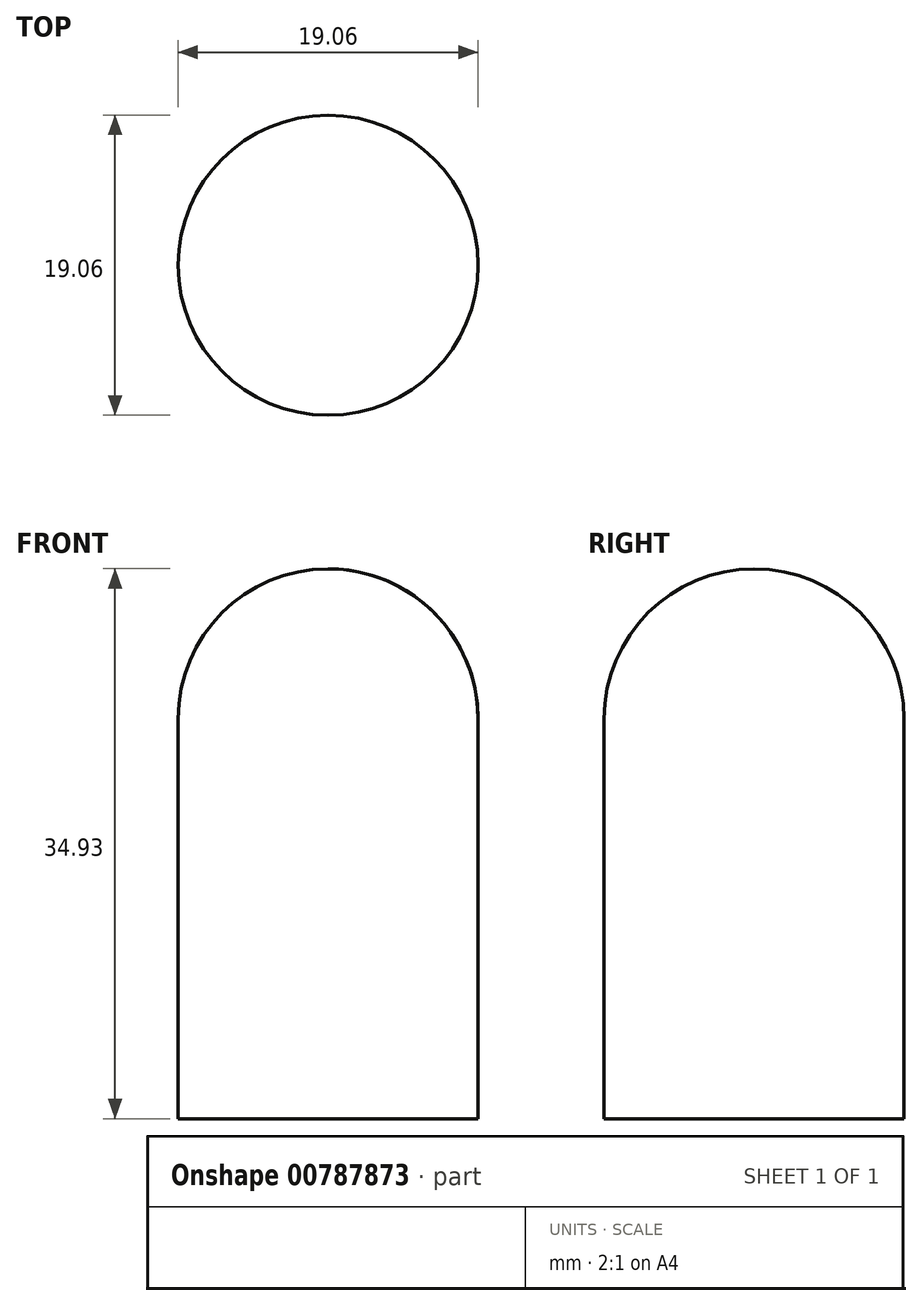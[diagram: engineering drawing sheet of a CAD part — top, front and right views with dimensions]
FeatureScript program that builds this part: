
annotation { "Feature Type Name" : "Feature", "Feature Type Description" : "" }
export const myFeature = defineFeature(function(context is Context, id is Id, definition is map)
    precondition{}
    {
        {
            var Q0;
            Q0=qCreatedBy(makeId("Front.planeOp"),FACE);
            var sketch = newSketch(context, id + "F0", { "sketchPlane" : qUnion([Q0])});
            skLineSegment(sketch, "E0", {"start": v(0, -40.89) * mm, "end": v(0, -15.49) * mm});
            skLineSegment(sketch, "E1", {"start": v(0, -15.49) * mm, "end": v(9.53, -15.49) * mm});
            skLineSegment(sketch, "E2", {"start": v(9.53, -15.49) * mm, "end": v(9.53, -40.89) * mm});
            skLineSegment(sketch, "E3", {"start": v(9.53, -40.89) * mm, "end": v(0, -40.89) * mm});
            skArc(sketch, "E4", {"start": v(9.53, -15.49) * mm, "mid": v(6.74, -8.75) * mm, "end": v(0, -5.96) * mm});
            skLineSegment(sketch, "E5", {"start": v(0, -5.96) * mm, "end": v(0, -15.49) * mm});
            skSolve(sketch);
        }
        {
            var Q0;
            Q0 = qSketchRegion(id + "F0", true);
            var Q1;
            Q1=sQuery(id+"F0.wireOp",EDGE,"E0");
            revolve(context, id + "F1", {"surfaceOperationType" : NewSurfaceOperationType.NEW, "entities" : qUnion([Q0]), "axis" : qUnion([Q1]), "revolveType" : RevolveType.FULL});
        }
    });
